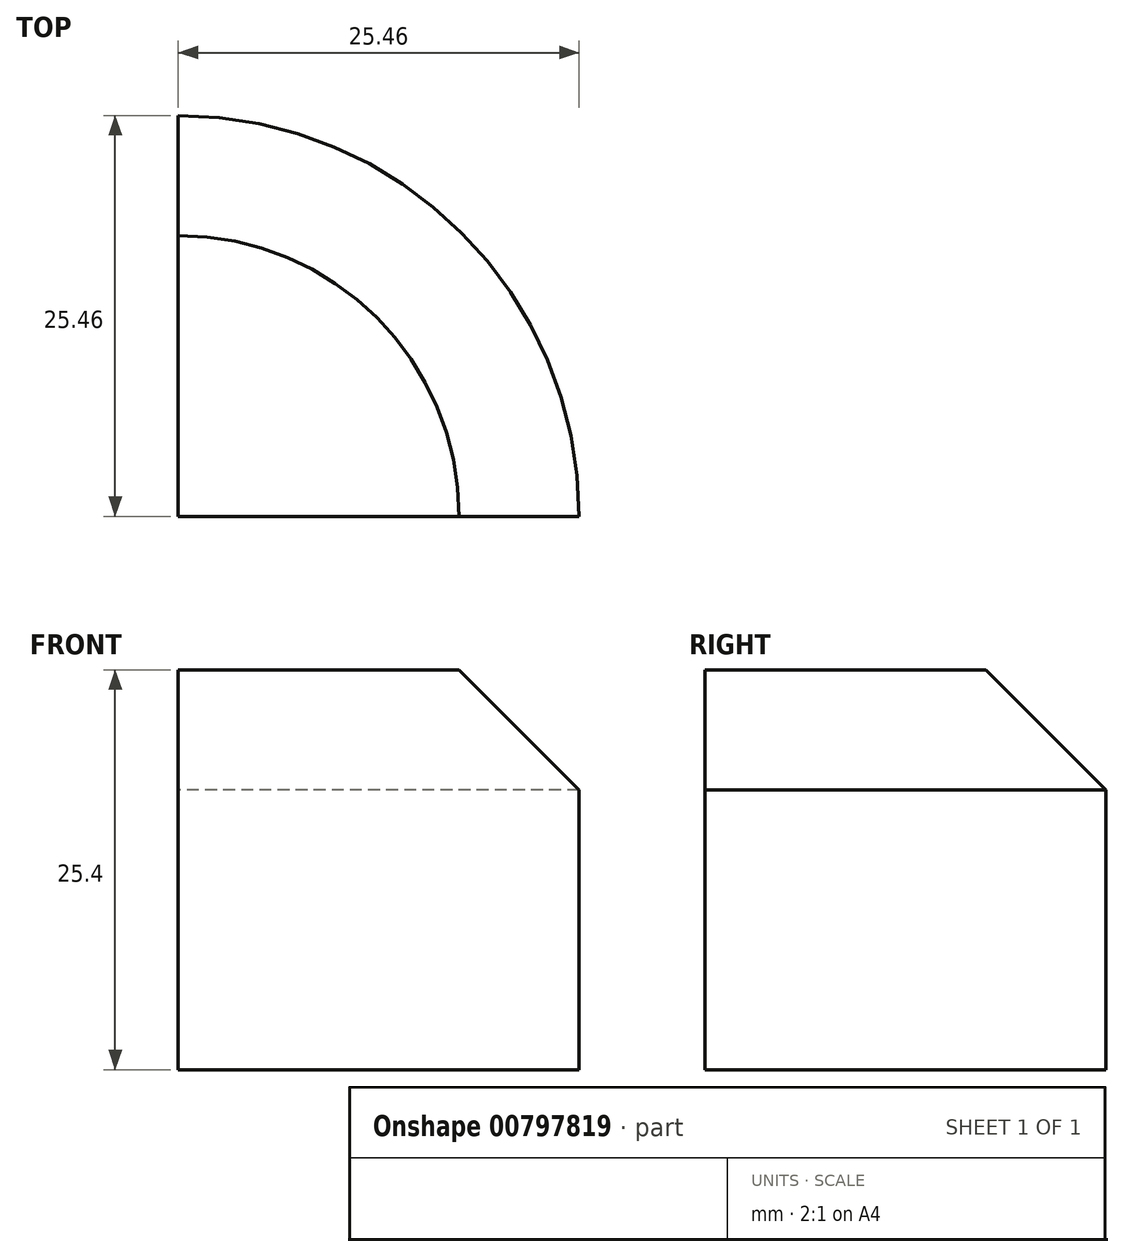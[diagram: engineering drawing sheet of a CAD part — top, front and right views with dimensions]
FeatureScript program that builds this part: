
annotation { "Feature Type Name" : "Feature", "Feature Type Description" : "" }
export const myFeature = defineFeature(function(context is Context, id is Id, definition is map)
    precondition{}
    {
        {
            var Q0;
            Q0=qCreatedBy(makeId("Top.planeOp"),FACE);
            var sketch = newSketch(context, id + "F0", { "sketchPlane" : qUnion([Q0])});
            skCircle(sketch, "E0", {"center": v(0, 0) * mm, "radius": 25.46 * mm});
            skLineSegment(sketch, "E1", {"start": v(0, 0) * mm, "end": v(0, 25.46) * mm});
            skLineSegment(sketch, "E2", {"start": v(0, 0) * mm, "end": v(25.46, 0) * mm});
            skSolve(sketch);
        }
        {
            var Q0;
            {var subQ0=sQuery(id+"F0.wireOp",EDGE,"E1");Q0=makeQuery(id+"F0.imprint","IMPRINT",FACE,{"disambiguationData":[TD([[makeQuery(id+"F0.imprint","IMPRINT",EDGE,{"derivedFrom":subQ0}),-1.0]])]});}
            extrude(context, id + "F1", {"entities" : qUnion([Q0]), "depth" : 25.4 * mm, "offsetDistance" : 25.4 * mm});
        }
        {
            var Q0;
            Q0=makeQuery(id+"F1.opExtrude","CAP_EDGE",EDGE,{"disambiguationData":[OSD([sQuery(id+"F0.wireOp",EDGE,"E0")])],"isStart":false});
            chamfer(context, id + "F2", {"entities" : qUnion([Q0]), "width" : 7.62 * mm, "tangentPropagation" : true});
        }
    });
